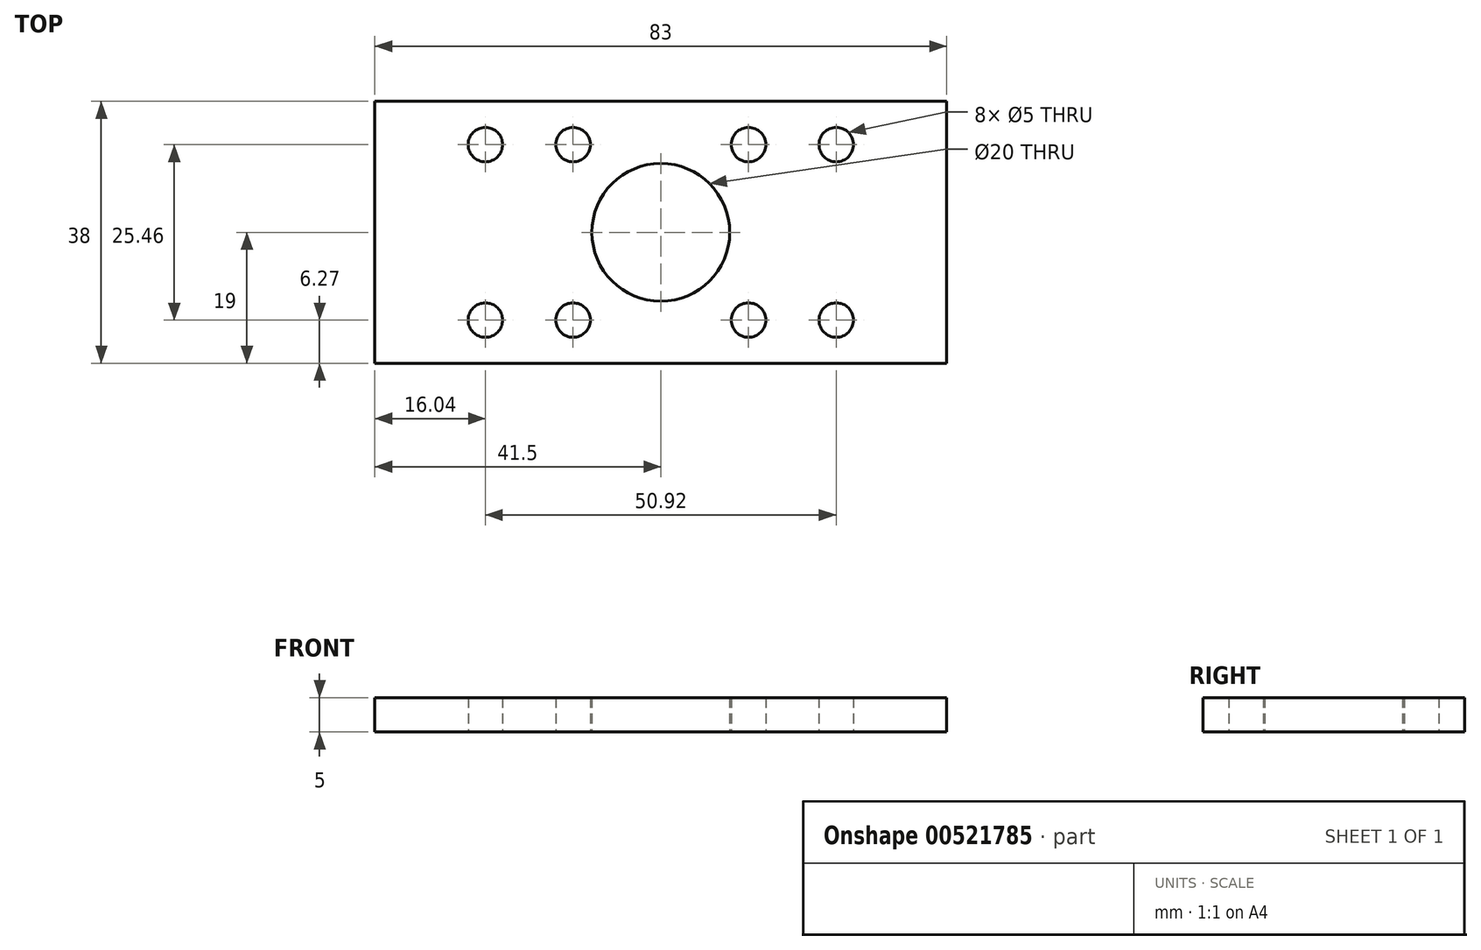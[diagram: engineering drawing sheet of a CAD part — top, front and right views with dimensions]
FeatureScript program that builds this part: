
annotation { "Feature Type Name" : "Feature", "Feature Type Description" : "" }
export const myFeature = defineFeature(function(context is Context, id is Id, definition is map)
    precondition{}
    {
        {
            var Q0;
            Q0=qCreatedBy(makeId("Top.planeOp"),FACE);
            var sketch = newSketch(context, id + "F0", { "sketchPlane" : qUnion([Q0])});
            skLineSegment(sketch, "E0.bottom", {"start": v(-41.5, -19) * mm, "end": v(41.5, -19) * mm});
            skLineSegment(sketch, "E0.top", {"start": v(-41.5, 19) * mm, "end": v(41.5, 19) * mm});
            skLineSegment(sketch, "E0.left", {"start": v(-41.5, -19) * mm, "end": v(-41.5, 19) * mm});
            skLineSegment(sketch, "E0.right", {"start": v(41.5, -19) * mm, "end": v(41.5, 19) * mm});
            skPoint(sketch, "E0.middle", {"position": v(0, 0) * mm});
            skCircle(sketch, "E1", {"center": v(0, 0) * mm, "radius": 10 * mm});
            skPoint(sketch, "E2", {"position": v(0, 12.73) * mm});
            skPoint(sketch, "E3", {"position": v(0, -12.73) * mm});
            skPoint(sketch, "E4", {"position": v(-12.73, 12.73) * mm});
            skPoint(sketch, "E5", {"position": v(-25.46, 12.73) * mm});
            skPoint(sketch, "E6", {"position": v(-12.73, -12.73) * mm});
            skPoint(sketch, "E7", {"position": v(-25.46, -12.73) * mm});
            skPoint(sketch, "E8", {"position": v(12.73, -12.73) * mm});
            skPoint(sketch, "E9", {"position": v(12.73, 12.73) * mm});
            skPoint(sketch, "E10", {"position": v(25.46, 12.73) * mm});
            skPoint(sketch, "E11", {"position": v(25.46, -12.73) * mm});
            skCircle(sketch, "E12", {"center": v(-25.46, 12.73) * mm, "radius": 2.5 * mm});
            skCircle(sketch, "E13", {"center": v(-12.73, 12.73) * mm, "radius": 2.5 * mm});
            skCircle(sketch, "E14", {"center": v(-25.46, -12.73) * mm, "radius": 2.5 * mm});
            skCircle(sketch, "E15", {"center": v(-12.73, -12.73) * mm, "radius": 2.5 * mm});
            skCircle(sketch, "E16", {"center": v(12.73, 12.73) * mm, "radius": 2.5 * mm});
            skCircle(sketch, "E17", {"center": v(25.46, 12.73) * mm, "radius": 2.5 * mm});
            skCircle(sketch, "E18", {"center": v(12.73, -12.73) * mm, "radius": 2.5 * mm});
            skCircle(sketch, "E19", {"center": v(25.46, -12.73) * mm, "radius": 2.5 * mm});
            skSolve(sketch);
        }
        {
            var Q0;
            Q0=makeQuery(id+"F0.imprint","IMPRINT",FACE,{"disambiguationData":[TD([[makeQuery(id+"F0.imprint","IMPRINT",EDGE,{"derivedFrom":sQuery(id+"F0.wireOp",EDGE,"E0.bottom")}),1.0]])]});
            extrude(context, id + "F1", {"entities" : qUnion([Q0]), "depth" : 5 * mm, "offsetDistance" : 25 * mm});
        }
    });
